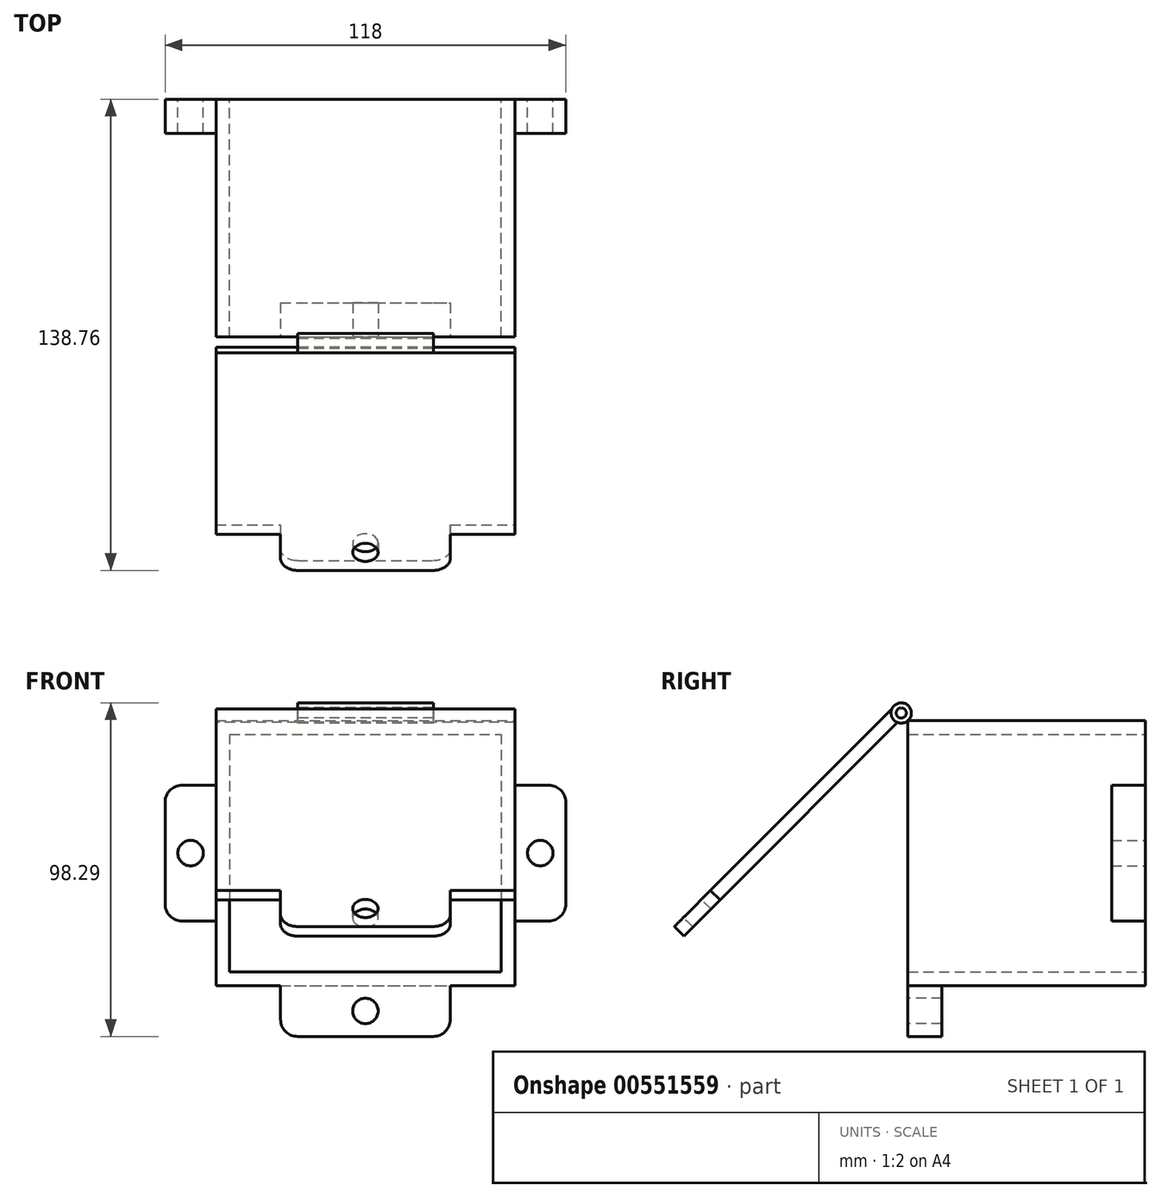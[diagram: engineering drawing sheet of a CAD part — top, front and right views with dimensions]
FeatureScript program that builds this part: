
annotation { "Feature Type Name" : "Feature", "Feature Type Description" : "" }
export const myFeature = defineFeature(function(context is Context, id is Id, definition is map)
    precondition{}
    {
        {
            var Q0;
            Q0=qCreatedBy(makeId("Front.planeOp"),FACE);
            var sketch = newSketch(context, id + "F0", { "sketchPlane" : qUnion([Q0])});
            skLineSegment(sketch, "E0.bottom", {"start": v(-40, 35) * mm, "end": v(40, 35) * mm});
            skLineSegment(sketch, "E0.top", {"start": v(-40, -35) * mm, "end": v(40, -35) * mm});
            skLineSegment(sketch, "E0.left", {"start": v(-40, 35) * mm, "end": v(-40, -35) * mm});
            skLineSegment(sketch, "E0.right", {"start": v(40, 35) * mm, "end": v(40, -35) * mm});
            skLineSegment(sketch, "E1.bottom", {"start": v(-44, 39) * mm, "end": v(44, 39) * mm});
            skLineSegment(sketch, "E1.top", {"start": v(-44, -39) * mm, "end": v(44, -39) * mm});
            skLineSegment(sketch, "E1.left", {"start": v(-44, 39) * mm, "end": v(-44, -39) * mm});
            skLineSegment(sketch, "E1.right", {"start": v(44, 39) * mm, "end": v(44, -39) * mm});
            skLineSegment(sketch, "E2", {"start": v(44, 20) * mm, "end": v(59, 20) * mm});
            skLineSegment(sketch, "E3", {"start": v(59, 20) * mm, "end": v(59, -20) * mm});
            skLineSegment(sketch, "E4", {"start": v(59, -20) * mm, "end": v(44, -20) * mm});
            skCircle(sketch, "E5", {"center": v(51.5, 0) * mm, "radius": 3.75 * mm});
            skSolve(sketch);
        }
        {
            var Q0;
            Q0=makeQuery(id+"F0.imprint","IMPRINT",FACE,{"disambiguationData":[TD([[makeQuery(id+"F0.imprint","IMPRINT",EDGE,{"derivedFrom":sQuery(id+"F0.wireOp",EDGE,"E0.bottom")}),1.0]])]});
            extrude(context, id + "F1", {"entities" : qUnion([Q0]), "depth" : 70 * mm, "offsetDistance" : 25 * mm});
        }
        {
            var Q0;
            {var subQ0=sQuery(id+"F0.wireOp",EDGE,"E2");Q0=makeQuery(id+"F0.imprint","IMPRINT",FACE,{"disambiguationData":[TD([[makeQuery(id+"F0.imprint","IMPRINT",EDGE,{"derivedFrom":subQ0}),-1.0]])]});}
            extrude(context, id + "F2", {"entities" : qUnion([Q0]), "operationType" : NewBodyOperationType.ADD, "depth" : 10 * mm, "offsetDistance" : 25 * mm});
        }
        {
            var Q0;
            Q0=makeQuery(id+"F2.opExtrude","SWEPT_EDGE",EDGE,{"disambiguationData":[OSD([sQuery(id+"F0.wireOp",EDGE,"E2"),sQuery(id+"F0.wireOp",EDGE,"E3")])]});
            var Q1;
            Q1=makeQuery(id+"F2.opExtrude","SWEPT_EDGE",EDGE,{"disambiguationData":[OSD([sQuery(id+"F0.wireOp",EDGE,"E3"),sQuery(id+"F0.wireOp",EDGE,"E4")])]});
            fillet(context, id + "F3", {"entities" : qUnion([Q0, Q1]), "radius" : 5 * mm, "tangentPropagation" : true, "allowEdgeOverflow" : false});
        }
        {
            var Q0;
            Q0=makeQuery(id+"F1.opExtrude","SWEPT_BODY",BODY,{"disambiguationData":[OSD([sQuery(id+"F0.wireOp",EDGE,"E0.bottom"),sQuery(id+"F0.wireOp",EDGE,"E0.top"),sQuery(id+"F0.wireOp",EDGE,"E0.left"),sQuery(id+"F0.wireOp",EDGE,"E0.right"),sQuery(id+"F0.wireOp",EDGE,"E1.bottom"),sQuery(id+"F0.wireOp",EDGE,"E1.top"),sQuery(id+"F0.wireOp",EDGE,"E1.left"),sQuery(id+"F0.wireOp",EDGE,"E1.right")])]});
            var Q1;
            Q1=qCreatedBy(makeId("Right.planeOp"),FACE);
            mirror(context, id + "F4", {"operationType" : NewBodyOperationType.ADD, "entities" : qUnion([Q0]), "mirrorPlane" : qUnion([Q1])});
        }
        {
            var Q0;
            Q0=makeQuery(id+"F1.opExtrude","CAP_FACE",FACE,{"disambiguationData":[OSD([sQuery(id+"F0.wireOp",EDGE,"E0.bottom"),sQuery(id+"F0.wireOp",EDGE,"E0.top"),sQuery(id+"F0.wireOp",EDGE,"E0.left"),sQuery(id+"F0.wireOp",EDGE,"E0.right"),sQuery(id+"F0.wireOp",EDGE,"E1.bottom"),sQuery(id+"F0.wireOp",EDGE,"E1.top"),sQuery(id+"F0.wireOp",EDGE,"E1.left"),sQuery(id+"F0.wireOp",EDGE,"E1.right")])],"isStart":false});
            var sketch = newSketch(context, id + "F5", { "sketchPlane" : qUnion([Q0])});
            skLineSegment(sketch, "E6", {"start": v(-30, 43) * mm, "end": v(-10, 43) * mm});
            skLineSegment(sketch, "E7", {"start": v(10, 43) * mm, "end": v(30, 43) * mm});
            skSolve(sketch);
        }
        {
            var Q0;
            Q0=makeQuery(id+"F5.imprint","IMPRINT",FACE,{"disambiguationData":[TD([[makeQuery(id+"F5.imprint","IMPRINT",EDGE,{"derivedFrom":makeQuery(id+"F1.opExtrude","CAP_EDGE",EDGE,{"disambiguationData":[OSD([sQuery(id+"F0.wireOp",EDGE,"E0.bottom")])],"isStart":false})}),1.0]])]});
            var sketch = newSketch(context, id + "F6", { "sketchPlane" : qUnion([Q0])});
            skLineSegment(sketch, "E8", {"start": v(-25, -39) * mm, "end": v(-25, -54) * mm});
            skLineSegment(sketch, "E9", {"start": v(-25, -54) * mm, "end": v(25, -54) * mm});
            skLineSegment(sketch, "E10", {"start": v(-25, -39) * mm, "end": v(25, -39) * mm});
            skLineSegment(sketch, "E11", {"start": v(25, -39) * mm, "end": v(25, -54) * mm});
            skCircle(sketch, "E12", {"center": v(0, -46.5) * mm, "radius": 3.75 * mm});
            skSolve(sketch);
        }
        {
            var Q0;
            Q0 = qSketchRegion(id + "F6", true);
            extrude(context, id + "F7", {"entities" : qUnion([Q0]), "operationType" : NewBodyOperationType.ADD, "oppositeDirection" : true, "depth" : 10 * mm, "offsetDistance" : 25 * mm});
        }
        {
            var Q0;
            Q0=makeQuery(id+"F7.opExtrude","SWEPT_EDGE",EDGE,{"disambiguationData":[OSD([sQuery(id+"F6.wireOp",EDGE,"E9"),sQuery(id+"F6.wireOp",EDGE,"E11")])]});
            var Q1;
            Q1=makeQuery(id+"F7.opExtrude","SWEPT_EDGE",EDGE,{"disambiguationData":[OSD([sQuery(id+"F6.wireOp",EDGE,"E8"),sQuery(id+"F6.wireOp",EDGE,"E9")])]});
            fillet(context, id + "F8", {"entities" : qUnion([Q0, Q1]), "radius" : 5 * mm, "tangentPropagation" : true, "allowEdgeOverflow" : false});
        }
        {
            var Q0;
            Q0=qCreatedBy(makeId("Right.planeOp"),FACE);
            var sketch = newSketch(context, id + "F9", { "sketchPlane" : qUnion([Q0])});
            skCircle(sketch, "E13", {"center": v(-71.94, 41.29) * mm, "radius": 3 * mm});
            skCircle(sketch, "E14", {"center": v(-71.94, 41.29) * mm, "radius": 1.5 * mm});
            skSolve(sketch);
        }
        {
            var Q0;
            Q0 = qSketchRegion(id + "F9", true);
            extrude(context, id + "F10", {"entities" : qUnion([Q0]), "endBound" : BoundingType.SYMMETRIC, "depth" : 40 * mm, "offsetDistance" : 25 * mm});
        }
        {
            var Q0;
            {var subQ0=sQuery(id+"F0.wireOp",EDGE,"E1.left");var subQ2=sQuery(id+"F0.wireOp",EDGE,"E1.top");Q0=makeQuery(id+"F7.boolean.opBoolean","SPLIT",EDGE,{"disambiguationData":[TD([makeQuery(id+"F1.opExtrude","SWEPT_FACE",FACE,{"disambiguationData":[OSD([subQ0])]})])],"derivedFrom":makeQuery(id+"F1.opExtrude","CAP_EDGE",EDGE,{"disambiguationData":[OSD([subQ2])],"isStart":false})});}
            cPlane(context, id + "F11", {"entities" : qUnion([Q0]), "cplaneType" : CPlaneType.LINE_ANGLE, "offset" : 25 * mm, "angle" : 45 * degree, "width" : 150 * mm, "height" : 150 * mm});
        }
        {
            var Q0;
            Q0=qCreatedBy(id+"F11.planeOp",FACE);
            var sketch = newSketch(context, id + "F12", { "sketchPlane" : qUnion([Q0])});
            skLineSegment(sketch, "E15.bottom", {"start": v(44, 82.83) * mm, "end": v(-44, 82.83) * mm});
            skLineSegment(sketch, "E15.top", {"start": v(44, 78.83) * mm, "end": v(-44, 78.83) * mm});
            skLineSegment(sketch, "E15.left", {"start": v(44, 82.83) * mm, "end": v(44, 78.83) * mm});
            skLineSegment(sketch, "E15.right", {"start": v(-44, 82.83) * mm, "end": v(-44, 78.83) * mm});
            skSolve(sketch);
        }
        {
            var Q0;
            Q0 = qSketchRegion(id + "F12", true);
            var Q1;
            Q1=makeQuery(id+"F10.opExtrude","SWEPT_FACE",FACE,{"disambiguationData":[OSD([sQuery(id+"F9.wireOp",EDGE,"E13")])]});
            extrude(context, id + "F13", {"entities" : qUnion([Q0]), "operationType" : NewBodyOperationType.ADD, "endBound" : BoundingType.UP_TO_SURFACE, "depth" : 25 * mm, "endBoundEntityFace" : qUnion([Q1]), "offsetDistance" : 25 * mm});
        }
        {
            var Q0;
            Q0=makeQuery(id+"F13.opExtrude","SWEPT_FACE",FACE,{"disambiguationData":[OSD([sQuery(id+"F12.wireOp",EDGE,"E15.bottom")])]});
            var sketch = newSketch(context, id + "F14", { "sketchPlane" : qUnion([Q0])});
            skLineSegment(sketch, "E16.bottom", {"start": v(-44, -77.07) * mm, "end": v(44, -77.07) * mm});
            skLineSegment(sketch, "E16.top", {"start": v(-44, -98.4) * mm, "end": v(-25, -98.4) * mm});
            skLineSegment(sketch, "E16.left", {"start": v(-44, -77.07) * mm, "end": v(-44, -98.4) * mm});
            skLineSegment(sketch, "E16.right", {"start": v(44, -77.07) * mm, "end": v(44, -98.4) * mm});
            skLineSegment(sketch, "E17", {"start": v(-25, -98.4) * mm, "end": v(-25, -113.4) * mm});
            skLineSegment(sketch, "E18", {"start": v(-25, -113.4) * mm, "end": v(25, -113.4) * mm});
            skLineSegment(sketch, "E19", {"start": v(25, -113.4) * mm, "end": v(25, -98.4) * mm});
            skLineSegment(sketch, "E20.trimOffspring", {"start": v(25, -98.4) * mm, "end": v(44, -98.4) * mm});
            skCircle(sketch, "E21", {"center": v(0, -105.9) * mm, "radius": 3.75 * mm});
            skSolve(sketch);
        }
        {
            var Q0;
            Q0 = qSketchRegion(id + "F14", true);
            extrude(context, id + "F15", {"entities" : qUnion([Q0]), "operationType" : NewBodyOperationType.ADD, "oppositeDirection" : true, "depth" : 4 * mm, "offsetDistance" : 25 * mm});
        }
        {
            var Q0;
            Q0=makeQuery(id+"F15.opExtrude","SWEPT_EDGE",EDGE,{"disambiguationData":[OSD([sQuery(id+"F14.wireOp",EDGE,"E18"),sQuery(id+"F14.wireOp",EDGE,"E19")])]});
            var Q1;
            Q1=makeQuery(id+"F15.opExtrude","SWEPT_EDGE",EDGE,{"disambiguationData":[OSD([sQuery(id+"F14.wireOp",EDGE,"E17"),sQuery(id+"F14.wireOp",EDGE,"E18")])]});
            fillet(context, id + "F16", {"entities" : qUnion([Q0, Q1]), "radius" : 5 * mm, "tangentPropagation" : true, "allowEdgeOverflow" : false});
        }
        {
            var Q0;
            Q0=makeQuery(id+"F10.opExtrude","SWEPT_BODY",BODY,{"disambiguationData":[OSD([sQuery(id+"F9.wireOp",EDGE,"E13"),sQuery(id+"F9.wireOp",EDGE,"E14")])]});
            var Q1;
            Q1=makeQuery(id+"F1.opExtrude","CAP_EDGE",EDGE,{"disambiguationData":[OSD([sQuery(id+"F0.wireOp",EDGE,"E1.bottom")])],"isStart":false});
            var Q2;
            Q2=makeQuery(id+"F10.opExtrude","CAP_EDGE",EDGE,{"disambiguationData":[OSD([sQuery(id+"F9.wireOp",EDGE,"E14")])],"isStart":true});
            transform(context, id + "F17", {"entities" : qUnion([Q0]), "transformType" : TransformType.ROTATION, "transformAxis" : qUnion([Q2]), "angle" : 0 * degree, "makeCopy" : false});
        }
    });
